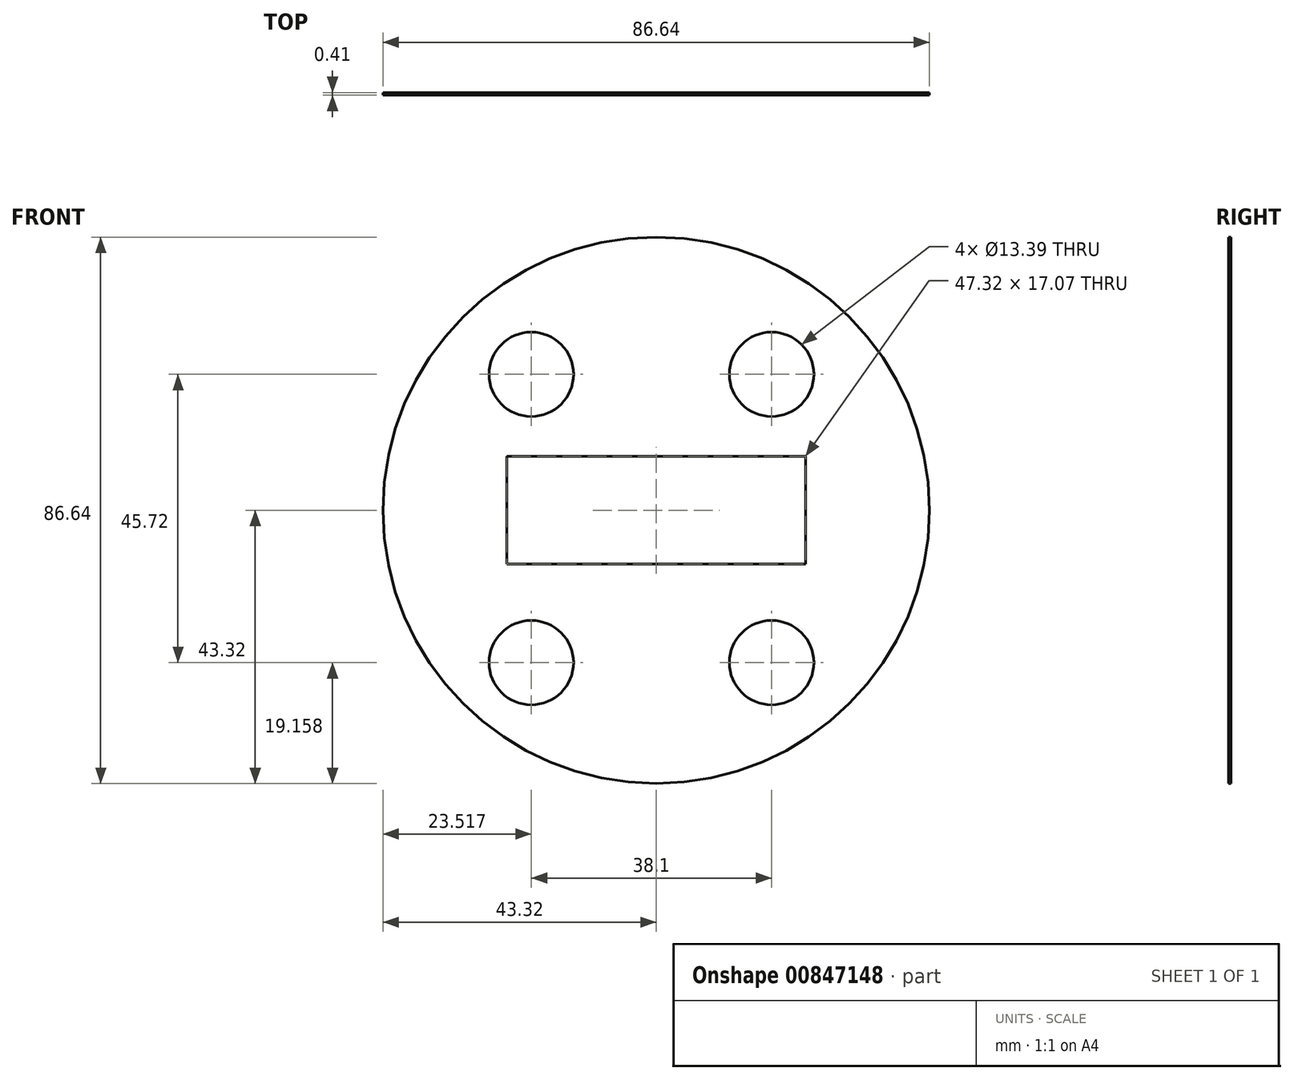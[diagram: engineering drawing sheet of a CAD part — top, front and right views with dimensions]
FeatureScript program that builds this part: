
annotation { "Feature Type Name" : "Feature", "Feature Type Description" : "" }
export const myFeature = defineFeature(function(context is Context, id is Id, definition is map)
    precondition{}
    {
        {
            var Q0;
            Q0=qCreatedBy(makeId("Front.planeOp"),FACE);
            var sketch = newSketch(context, id + "F0", { "sketchPlane" : qUnion([Q0])});
            skCircle(sketch, "E0", {"center": v(0, 0) * mm, "radius": 43.32 * mm});
            skLineSegment(sketch, "E1.bottom", {"start": v(-23.66, 8.53) * mm, "end": v(23.66, 8.53) * mm});
            skLineSegment(sketch, "E1.top", {"start": v(-23.66, -8.53) * mm, "end": v(23.66, -8.53) * mm});
            skLineSegment(sketch, "E1.left", {"start": v(-23.66, 8.53) * mm, "end": v(-23.66, -8.53) * mm});
            skLineSegment(sketch, "E1.right", {"start": v(23.66, 8.53) * mm, "end": v(23.66, -8.53) * mm});
            skCircle(sketch, "E2", {"center": v(-123.3, -44.07) * mm, "radius": 6.5 * mm, "construction": true});
            skCircle(sketch, "E3", {"center": v(-40.79, -50.52) * mm, "radius": 3.78 * mm});
            skCircle(sketch, "E4", {"center": v(-95.9, -98.27) * mm, "radius": 3.73 * mm});
            skCircle(sketch, "E5", {"center": v(18.3, -24.16) * mm, "radius": 6.7 * mm});
            skLineSegment(sketch, "E6", {"start": v(0, 43.32) * mm, "end": v(0, 22.55) * mm});
            skPoint(sketch, "E6.startSnap0", {"position": v(0, 8.53) * mm});
            skPoint(sketch, "E6.endSnap0", {"position": v(0, 8.53) * mm});
            skLineSegment(sketch, "E7", {"start": v(0, 22.55) * mm, "end": v(0, 32.94) * mm, "construction": true});
            skCircle(sketch, "E8.0.1.0", {"center": v(18.3, 21.56) * mm, "radius": 6.7 * mm});
            skCircle(sketch, "E8.1.0.0", {"center": v(-19.8, -24.16) * mm, "radius": 6.7 * mm});
            skCircle(sketch, "E8.1.1.0", {"center": v(-19.8, 21.56) * mm, "radius": 6.7 * mm});
            skLineSegment(sketch, "E8.direction1", {"start": v(18.3, -24.16) * mm, "end": v(-19.8, -24.16) * mm, "construction": true});
            skLineSegment(sketch, "E8.direction2", {"start": v(18.3, -24.16) * mm, "end": v(18.3, 21.56) * mm, "construction": true});
            skSolve(sketch);
        }
        {
            var Q0;
            Q0=makeQuery(id+"F0.imprint","IMPRINT",FACE,{"disambiguationData":[TD([[makeQuery(id+"F0.imprint","IMPRINT",EDGE,{"derivedFrom":sQuery(id+"F0.wireOp",EDGE,"E0")}),1.0]])]});
            extrude(context, id + "F1", {"entities" : qUnion([Q0]), "depth" : -0.4 * mm, "offsetDistance" : 25.4 * mm});
        }
    });
